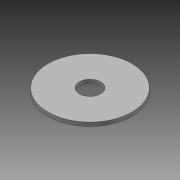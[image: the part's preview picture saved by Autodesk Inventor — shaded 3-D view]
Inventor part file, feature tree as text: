
AUTODESK INVENTOR PART (.ipt)
format: ipt  version: 2014 SP1 (Build 180222100, 222)  size: 74,752 bytes
history: native  units: in
note: dims shown in document units (in); Inventor stores cm internally (conversion verified against a paired STEP export)
features: extrude x1, sketch x1
ambient origin geometry x8: Origin, YZ Plane, XZ Plane, XY Plane, X Axis, Y Axis, Z Axis, Center Point
bodies: Solid1 (feature_tree)
feature tree (2):
  extrude  "Extrusion1"  Depth=0.05in
  sketch  "Sketch1"  dims[d0=0.2812in d1=1.125in d2=0.05in d3=0.0in]
